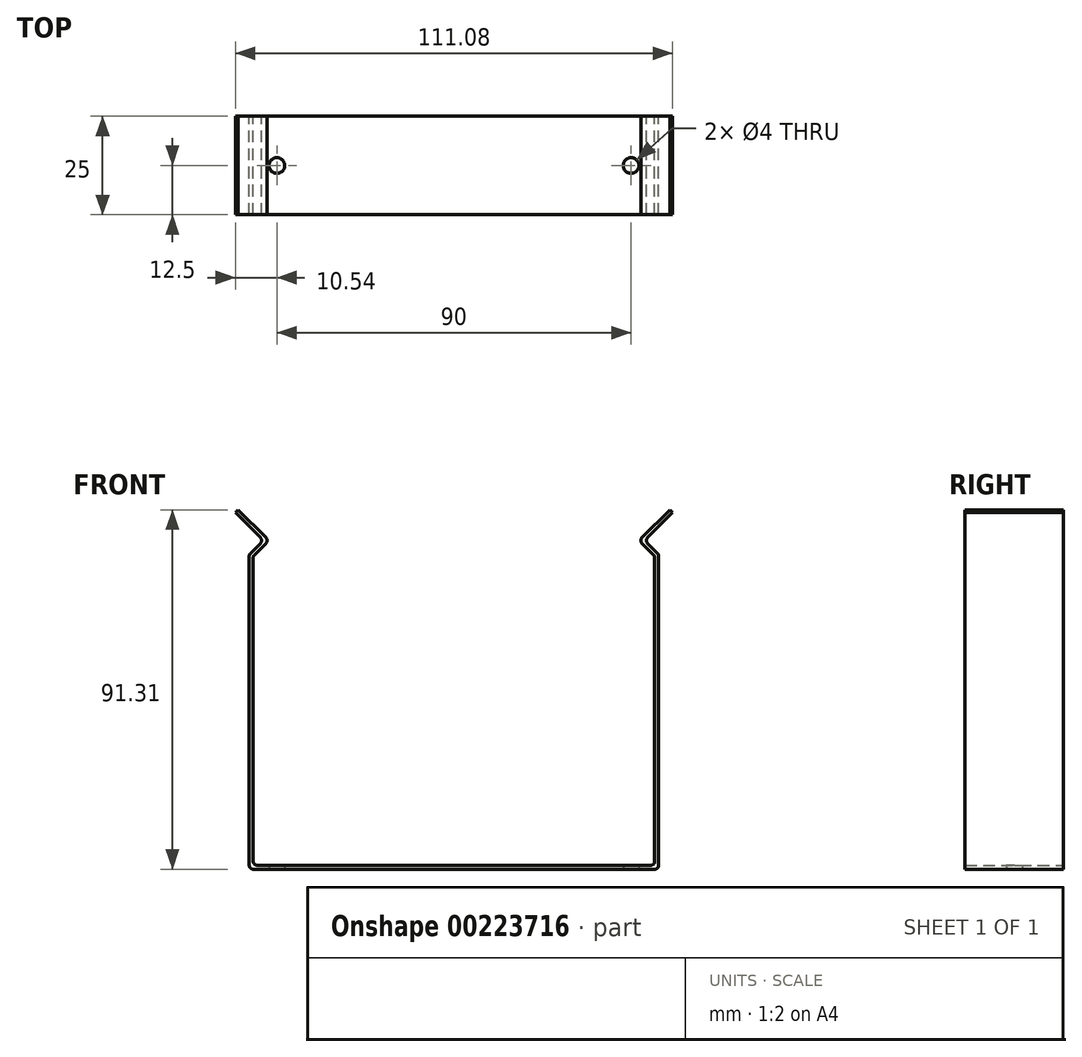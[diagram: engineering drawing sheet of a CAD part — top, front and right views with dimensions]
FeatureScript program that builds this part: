
annotation { "Feature Type Name" : "Feature", "Feature Type Description" : "" }
export const myFeature = defineFeature(function(context is Context, id is Id, definition is map)
    precondition{}
    {
        {
            var Q0;
            Q0=qCreatedBy(makeId("Front.planeOp"),FACE);
            var sketch = newSketch(context, id + "F0", { "sketchPlane" : qUnion([Q0])});
            skLineSegment(sketch, "E0", {"start": v(0, 0) * mm, "end": v(-51, 0) * mm});
            skLineSegment(sketch, "E1", {"start": v(-52, 1) * mm, "end": v(-52, 79.59) * mm});
            skLineSegment(sketch, "E2", {"start": v(-51.7, 80.3) * mm, "end": v(-49.17, 82.83) * mm});
            skLineSegment(sketch, "E3", {"start": v(-49.17, 84.24) * mm, "end": v(-52, 87.07) * mm});
            skLineSegment(sketch, "E4", {"start": v(-52, 87.07) * mm, "end": v(-55.54, 90.6) * mm});
            skLineSegment(sketch, "E5", {"start": v(-55.54, 90.6) * mm, "end": v(-54.83, 91.31) * mm});
            skLineSegment(sketch, "E6", {"start": v(-54.83, 91.31) * mm, "end": v(-47.76, 84.24) * mm});
            skLineSegment(sketch, "E7", {"start": v(-47.76, 82.83) * mm, "end": v(-50.59, 80) * mm});
            skLineSegment(sketch, "E8", {"start": v(-51, 79.17) * mm, "end": v(-51, 2) * mm});
            skLineSegment(sketch, "E9", {"start": v(0, 1) * mm, "end": v(-50, 1) * mm});
            skLineSegment(sketch, "E10", {"start": v(-50.7, 79.88) * mm, "end": v(-50.59, 80) * mm});
            skPoint(sketch, "E11.visualSharp", {"position": v(-48.46, 83.54) * mm});
            skArc(sketch, "E11.filletArc", {"start": v(-49.17, 82.83) * mm, "mid": v(-48.88, 83.54) * mm, "end": v(-49.17, 84.24) * mm});
            skPoint(sketch, "E12.visualSharp", {"position": v(-47.05, 83.54) * mm});
            skArc(sketch, "E12.filletArc", {"start": v(-47.76, 82.83) * mm, "mid": v(-47.46, 83.54) * mm, "end": v(-47.76, 84.24) * mm});
            skPoint(sketch, "E13.visualSharp", {"position": v(-51, 79.59) * mm});
            skArc(sketch, "E13.filletArc", {"start": v(-50.7, 79.88) * mm, "mid": v(-50.92, 79.55) * mm, "end": v(-51, 79.17) * mm});
            skPoint(sketch, "E14.visualSharp", {"position": v(-52, 80) * mm});
            skArc(sketch, "E14.filletArc", {"start": v(-51.7, 80.3) * mm, "mid": v(-51.92, 79.97) * mm, "end": v(-52, 79.59) * mm});
            skPoint(sketch, "E15.visualSharp", {"position": v(-51, 1) * mm});
            skArc(sketch, "E15.filletArc", {"start": v(-51, 2) * mm, "mid": v(-50.7, 1.3) * mm, "end": v(-50, 1) * mm});
            skPoint(sketch, "E16.visualSharp", {"position": v(-52, 0) * mm});
            skArc(sketch, "E16.filletArc", {"start": v(-52, 1) * mm, "mid": v(-51.7, 0.3) * mm, "end": v(-51, 0) * mm});
            skLineSegment(sketch, "E17.MirrorCS", {"start": v(50.7, 79.88) * mm, "end": v(50.59, 80) * mm});
            skArc(sketch, "E18.MirrorCS", {"start": v(50.7, 79.88) * mm, "mid": v(50.92, 79.55) * mm, "end": v(51, 79.17) * mm});
            skArc(sketch, "E19.MirrorCS", {"start": v(51.7, 80.3) * mm, "mid": v(51.92, 79.97) * mm, "end": v(52, 79.59) * mm});
            skLineSegment(sketch, "E20.MirrorCS", {"start": v(47.76, 82.83) * mm, "end": v(50.59, 80) * mm});
            skArc(sketch, "E21.MirrorCS", {"start": v(49.17, 82.83) * mm, "mid": v(48.88, 83.54) * mm, "end": v(49.17, 84.24) * mm});
            skArc(sketch, "E22.MirrorCS", {"start": v(47.76, 82.83) * mm, "mid": v(47.46, 83.54) * mm, "end": v(47.76, 84.24) * mm});
            skLineSegment(sketch, "E23.MirrorCS", {"start": v(51.7, 80.3) * mm, "end": v(49.17, 82.83) * mm});
            skArc(sketch, "E24.MirrorCS", {"start": v(52, 1) * mm, "mid": v(51.7, 0.3) * mm, "end": v(51, 0) * mm});
            skArc(sketch, "E25.MirrorCS", {"start": v(51, 2) * mm, "mid": v(50.7, 1.3) * mm, "end": v(50, 1) * mm});
            skLineSegment(sketch, "E26.MirrorCS", {"start": v(49.17, 84.24) * mm, "end": v(52, 87.07) * mm});
            skLineSegment(sketch, "E27.MirrorCS", {"start": v(55.54, 90.6) * mm, "end": v(54.83, 91.31) * mm});
            skLineSegment(sketch, "E28.MirrorCS", {"start": v(52, 87.07) * mm, "end": v(55.54, 90.6) * mm});
            skLineSegment(sketch, "E29.MirrorCS", {"start": v(51, 79.17) * mm, "end": v(51, 2) * mm});
            skPoint(sketch, "E30.MirrorP", {"position": v(47.05, 83.54) * mm});
            skPoint(sketch, "E31.MirrorP", {"position": v(52, 80) * mm});
            skLineSegment(sketch, "E32.MirrorCS", {"start": v(0, 1) * mm, "end": v(50, 1) * mm});
            skLineSegment(sketch, "E33.MirrorCS", {"start": v(0, 0) * mm, "end": v(51, 0) * mm});
            skPoint(sketch, "E34.MirrorP", {"position": v(52, 0) * mm});
            skLineSegment(sketch, "E35.MirrorCS", {"start": v(52, 1) * mm, "end": v(52, 79.59) * mm});
            skLineSegment(sketch, "E36.MirrorCS", {"start": v(54.83, 91.31) * mm, "end": v(47.76, 84.24) * mm});
            skSolve(sketch);
        }
        {
            var Q0;
            Q0=qSketchRegion(id+"F0",true);
            extrude(context, id + "F1", {"entities" : qUnion([Q0]), "depth" : 25 * mm});
        }
        {
            var Q0;
            Q0=qCreatedBy(makeId("Top.planeOp"),FACE);
            var sketch = newSketch(context, id + "F2", { "sketchPlane" : qUnion([Q0])});
            skPoint(sketch, "E37", {"position": v(-45, -12.5) * mm});
            skPoint(sketch, "E38.MirrorP", {"position": v(45, -12.5) * mm});
            skSolve(sketch);
        }
        {
            var Q0;
            Q0=sQuery(id+"F2.wireOp",VERTEX,"E37");
            var Q1;
            Q1=sQuery(id+"F2.wireOp",VERTEX,"E38.MirrorP");
            var Q2;
            Q2=makeQuery(id+"F1.opExtrude","SWEPT_BODY",BODY,{"disambiguationData":[OSD([sQuery(id+"F0.wireOp",EDGE,"E0"),sQuery(id+"F0.wireOp",EDGE,"E1"),sQuery(id+"F0.wireOp",EDGE,"E2"),sQuery(id+"F0.wireOp",EDGE,"E3"),sQuery(id+"F0.wireOp",EDGE,"E4"),sQuery(id+"F0.wireOp",EDGE,"E5"),sQuery(id+"F0.wireOp",EDGE,"E6"),sQuery(id+"F0.wireOp",EDGE,"E7"),sQuery(id+"F0.wireOp",EDGE,"E8"),sQuery(id+"F0.wireOp",EDGE,"E9"),sQuery(id+"F0.wireOp",EDGE,"E10"),sQuery(id+"F0.wireOp",EDGE,"E11.filletArc"),sQuery(id+"F0.wireOp",EDGE,"E12.filletArc"),sQuery(id+"F0.wireOp",EDGE,"E13.filletArc"),sQuery(id+"F0.wireOp",EDGE,"E14.filletArc"),sQuery(id+"F0.wireOp",EDGE,"E15.filletArc"),sQuery(id+"F0.wireOp",EDGE,"E16.filletArc"),sQuery(id+"F0.wireOp",EDGE,"E17.MirrorCS"),sQuery(id+"F0.wireOp",EDGE,"E18.MirrorCS"),sQuery(id+"F0.wireOp",EDGE,"E19.MirrorCS"),sQuery(id+"F0.wireOp",EDGE,"E20.MirrorCS"),sQuery(id+"F0.wireOp",EDGE,"E21.MirrorCS"),sQuery(id+"F0.wireOp",EDGE,"E22.MirrorCS"),sQuery(id+"F0.wireOp",EDGE,"E23.MirrorCS"),sQuery(id+"F0.wireOp",EDGE,"E24.MirrorCS"),sQuery(id+"F0.wireOp",EDGE,"E25.MirrorCS"),sQuery(id+"F0.wireOp",EDGE,"E26.MirrorCS"),sQuery(id+"F0.wireOp",EDGE,"E27.MirrorCS"),sQuery(id+"F0.wireOp",EDGE,"E28.MirrorCS"),sQuery(id+"F0.wireOp",EDGE,"E29.MirrorCS"),sQuery(id+"F0.wireOp",EDGE,"E32.MirrorCS"),sQuery(id+"F0.wireOp",EDGE,"E33.MirrorCS"),sQuery(id+"F0.wireOp",EDGE,"E35.MirrorCS"),sQuery(id+"F0.wireOp",EDGE,"E36.MirrorCS")])]});
            hole(context, id + "F3", {"style" : HoleStyle.SIMPLE, "endStyle" : HoleEndStyle.BLIND, "oppositeDirection" : true, "holeDiameter" : 4 * mm, "holeDepth" : 12 * mm, "locations" : qUnion([Q0, Q1]), "scope" : qUnion([Q2])});
        }
    });
